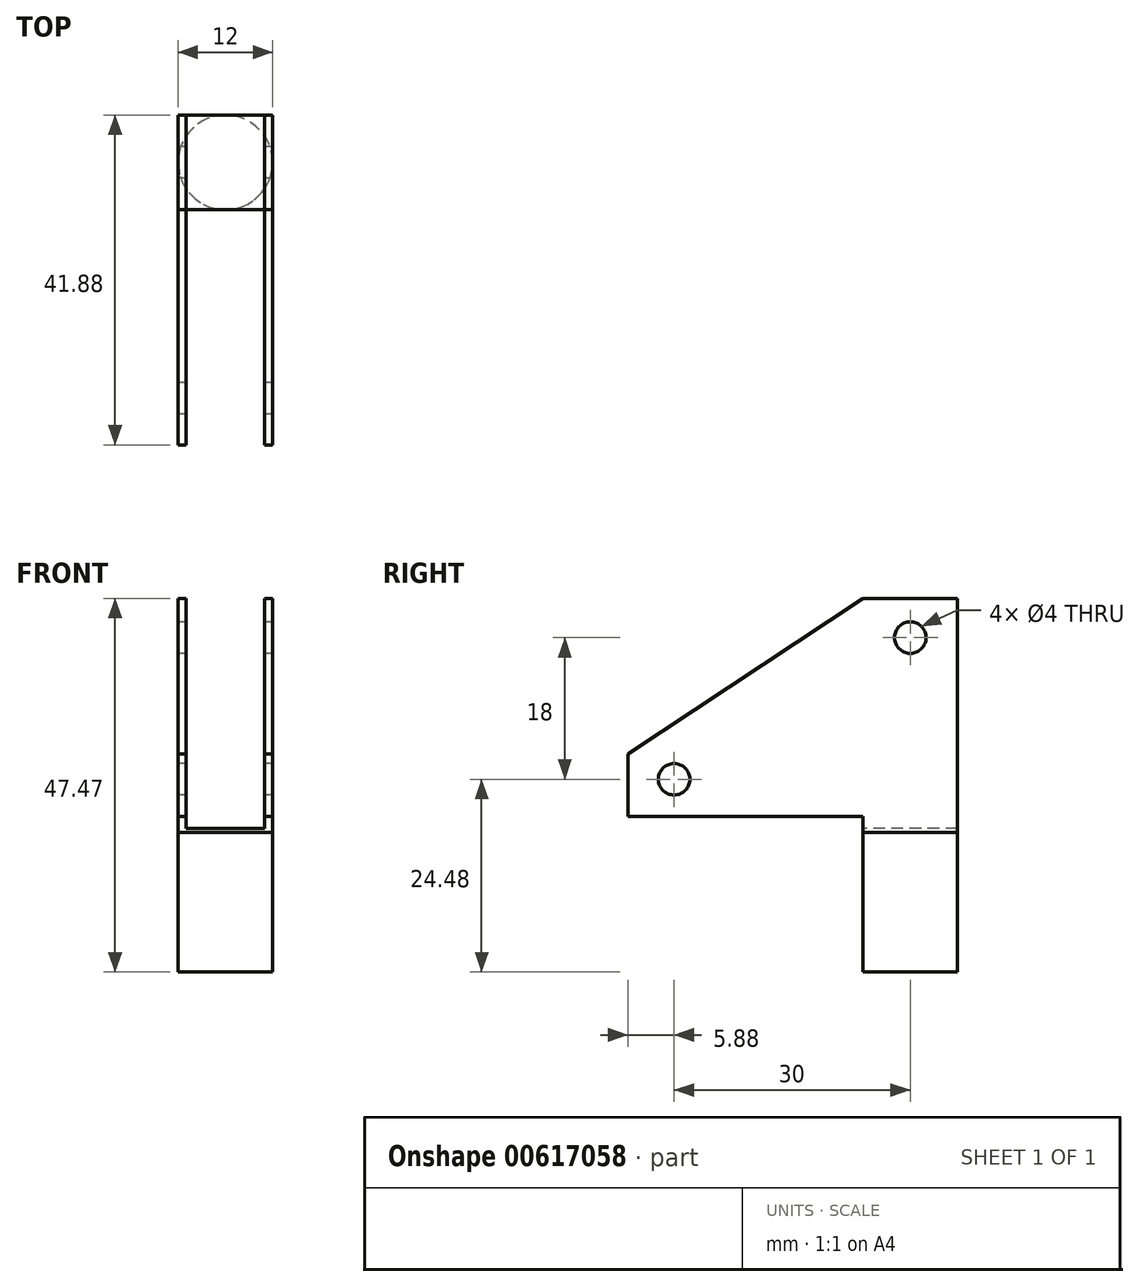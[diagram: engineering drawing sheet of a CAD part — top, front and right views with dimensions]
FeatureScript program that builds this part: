
annotation { "Feature Type Name" : "Feature", "Feature Type Description" : "" }
export const myFeature = defineFeature(function(context is Context, id is Id, definition is map)
    precondition{}
    {
        {
            var Q0;
            Q0=qCreatedBy(makeId("Right.planeOp"),FACE);
            var sketch = newSketch(context, id + "F0", { "sketchPlane" : qUnion([Q0])});
            skCircle(sketch, "E0", {"center": v(0, 0) * mm, "radius": 2 * mm});
            skCircle(sketch, "E1", {"center": v(-30, -18) * mm, "radius": 2 * mm});
            skLineSegment(sketch, "E2", {"start": v(-35.88, -14.75) * mm, "end": v(-35.88, -22.75) * mm});
            skLineSegment(sketch, "E3", {"start": v(-35.88, -22.75) * mm, "end": v(-6, -22.75) * mm});
            skLineSegment(sketch, "E4", {"start": v(-6, -22.75) * mm, "end": v(-6, -42.48) * mm});
            skLineSegment(sketch, "E5", {"start": v(-6, -42.48) * mm, "end": v(6, -42.48) * mm});
            skLineSegment(sketch, "E6", {"start": v(6, -42.48) * mm, "end": v(6, 4.99) * mm});
            skLineSegment(sketch, "E7", {"start": v(6, 4.99) * mm, "end": v(-6, 4.99) * mm});
            skLineSegment(sketch, "E8", {"start": v(-6, 4.99) * mm, "end": v(-35.88, -14.75) * mm});
            skSolve(sketch);
        }
        {
            var Q0;
            Q0 = qSketchRegion(id + "F0", true);
            extrude(context, id + "F1", {"entities" : qUnion([Q0]), "endBound" : BoundingType.SYMMETRIC, "depth" : 12 * mm, "offsetDistance" : 25 * mm});
        }
        {
            var Q0;
            Q0=qCreatedBy(makeId("Front.planeOp"),FACE);
            var sketch = newSketch(context, id + "F2", { "sketchPlane" : qUnion([Q0])});
            skLineSegment(sketch, "E9.bottom", {"start": v(5, -24.22) * mm, "end": v(-5, -24.22) * mm});
            skLineSegment(sketch, "E9.top", {"start": v(5, 9.77) * mm, "end": v(-5, 9.77) * mm});
            skLineSegment(sketch, "E9.left", {"start": v(5, -24.22) * mm, "end": v(5, 9.77) * mm});
            skLineSegment(sketch, "E9.right", {"start": v(-5, -24.22) * mm, "end": v(-5, 9.77) * mm});
            skPoint(sketch, "E9.middle", {"position": v(0, -7.23) * mm});
            skSolve(sketch);
        }
        {
            var Q0;
            Q0 = qSketchRegion(id + "F2", true);
            extrude(context, id + "F3", {"entities" : qUnion([Q0]), "operationType" : NewBodyOperationType.REMOVE, "endBound" : BoundingType.THROUGH_ALL, "oppositeDirection" : true, "depth" : 25 * mm, "offsetDistance" : 25 * mm, "hasSecondDirection" : true, "secondDirectionBound" : SecondDirectionBoundingType.THROUGH_ALL, "secondDirectionOppositeDirection" : false, "secondDirectionDepth" : 25 * mm});
        }
        {
            var Q0;
            Q0=makeQuery(id+"F1.opExtrude","SWEPT_FACE",FACE,{"disambiguationData":[OSD([sQuery(id+"F0.wireOp",EDGE,"E5")])]});
            var sketch = newSketch(context, id + "F4", { "sketchPlane" : qUnion([Q0])});
            skCircle(sketch, "E10", {"center": v(0, 0) * mm, "radius": 6 * mm});
            skLineSegment(sketch, "E11.bottom", {"start": v(9.5, -8.73) * mm, "end": v(-9.5, -8.73) * mm});
            skLineSegment(sketch, "E11.top", {"start": v(9.5, 8.73) * mm, "end": v(-9.5, 8.73) * mm});
            skLineSegment(sketch, "E11.left", {"start": v(9.5, -8.73) * mm, "end": v(9.5, 8.73) * mm});
            skLineSegment(sketch, "E11.right", {"start": v(-9.5, -8.73) * mm, "end": v(-9.5, 8.73) * mm});
            skSolve(sketch);
        }
        {
            var Q0;
            {var subQ0=sQuery(id+"F4.wireOp",EDGE,"E10");var subQ1=sQuery(id+"F0.wireOp",EDGE,"E5");var subQ2=makeQuery(id+"F1.opExtrude","CAP_EDGE",EDGE,{"disambiguationData":[OSD([subQ1])],"isStart":true});var subQ3=makeQuery(id+"F4.imprint","INTERSECT",VERTEX,{"derivedFrom":[subQ2,subQ0]});Q0=makeQuery(id+"F4.imprint","IMPRINT",FACE,{"disambiguationData":[TD([[makeQuery(id+"F4.imprint","IMPRINT",EDGE,{"disambiguationData":[TD([[subQ3,-1.0]])],"derivedFrom":subQ0}),-1.0]])]});}
            var Q1;
            {var subQ0=sQuery(id+"F4.wireOp",EDGE,"E10");var subQ1=sQuery(id+"F0.wireOp",EDGE,"E5");var subQ4=makeQuery(id+"F1.opExtrude","CAP_EDGE",EDGE,{"disambiguationData":[OSD([subQ1])],"isStart":true});var subQ5=makeQuery(id+"F4.imprint","INTERSECT",VERTEX,{"derivedFrom":[subQ4,subQ0]});Q1=makeQuery(id+"F4.imprint","IMPRINT",FACE,{"disambiguationData":[TD([[makeQuery(id+"F4.imprint","IMPRINT",EDGE,{"disambiguationData":[TD([[subQ5,1.0]])],"derivedFrom":subQ0}),-1.0]])]});}
            var Q2;
            {var subQ0=sQuery(id+"F4.wireOp",EDGE,"E10");var subQ1=sQuery(id+"F0.wireOp",EDGE,"E5");var subQ4=makeQuery(id+"F1.opExtrude","CAP_EDGE",EDGE,{"disambiguationData":[OSD([subQ1])],"isStart":false});var subQ5=makeQuery(id+"F4.imprint","INTERSECT",VERTEX,{"derivedFrom":[subQ4,subQ0]});Q2=makeQuery(id+"F4.imprint","IMPRINT",FACE,{"disambiguationData":[TD([[makeQuery(id+"F4.imprint","IMPRINT",EDGE,{"disambiguationData":[TD([[subQ5,-1.0]])],"derivedFrom":subQ0}),-1.0]])]});}
            var Q3;
            {var subQ0=sQuery(id+"F4.wireOp",EDGE,"E10");var subQ1=sQuery(id+"F0.wireOp",EDGE,"E5");var subQ2=makeQuery(id+"F1.opExtrude","CAP_EDGE",EDGE,{"disambiguationData":[OSD([subQ1])],"isStart":false});var subQ3=makeQuery(id+"F4.imprint","INTERSECT",VERTEX,{"derivedFrom":[subQ2,subQ0]});Q3=makeQuery(id+"F4.imprint","IMPRINT",FACE,{"disambiguationData":[TD([[makeQuery(id+"F4.imprint","IMPRINT",EDGE,{"disambiguationData":[TD([[subQ3,1.0]])],"derivedFrom":subQ0}),-1.0]])]});}
            extrude(context, id + "F5", {"entities" : qUnion([Q0, Q1, Q2, Q3]), "operationType" : NewBodyOperationType.REMOVE, "oppositeDirection" : true, "depth" : 17.7 * mm, "offsetDistance" : 25 * mm});
        }
    });
